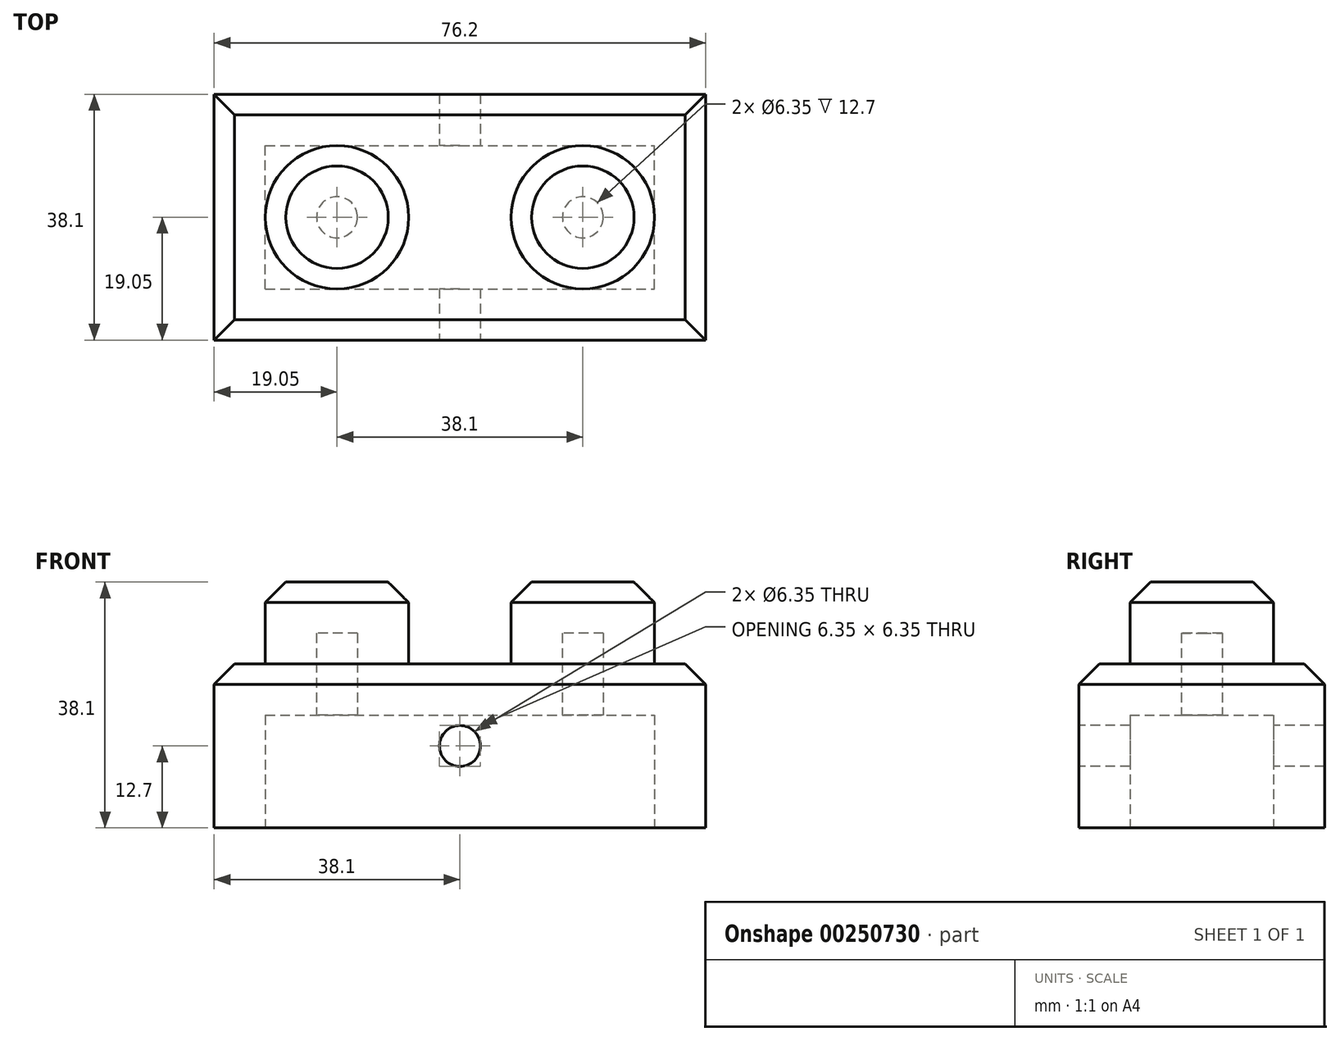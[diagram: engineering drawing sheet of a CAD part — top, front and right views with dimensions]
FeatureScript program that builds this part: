
annotation { "Feature Type Name" : "Feature", "Feature Type Description" : "" }
export const myFeature = defineFeature(function(context is Context, id is Id, definition is map)
    precondition{}
    {
        {
            var Q0;
            Q0=qCreatedBy(makeId("Top.planeOp"),FACE);
            var sketch = newSketch(context, id + "F0", { "sketchPlane" : qUnion([Q0])});
            skLineSegment(sketch, "E0.bottom", {"start": v(0, 0) * mm, "end": v(76.2, 0) * mm});
            skLineSegment(sketch, "E0.top", {"start": v(0, 38.1) * mm, "end": v(76.2, 38.1) * mm});
            skLineSegment(sketch, "E0.left", {"start": v(0, 0) * mm, "end": v(0, 38.1) * mm});
            skLineSegment(sketch, "E0.right", {"start": v(76.2, 0) * mm, "end": v(76.2, 38.1) * mm});
            skSolve(sketch);
        }
        {
            var Q0;
            Q0=makeQuery(id+"F0.imprint","IMPRINT",FACE,{"disambiguationData":[TD([[makeQuery(id+"F0.imprint","IMPRINT",EDGE,{"derivedFrom":sQuery(id+"F0.wireOp",EDGE,"E0.bottom")}),1.0]])]});
            extrude(context, id + "F1", {"entities" : qUnion([Q0]), "depth" : 25.4 * mm});
        }
        {
            var Q0;
            Q0=makeQuery(id+"F1.opExtrude","CAP_FACE",FACE,{"disambiguationData":[OSD([sQuery(id+"F0.wireOp",EDGE,"E0.bottom"),sQuery(id+"F0.wireOp",EDGE,"E0.top"),sQuery(id+"F0.wireOp",EDGE,"E0.left"),sQuery(id+"F0.wireOp",EDGE,"E0.right")])],"isStart":false});
            var sketch = newSketch(context, id + "F2", { "sketchPlane" : qUnion([Q0])});
            skCircle(sketch, "E1", {"center": v(19.05, 19.05) * mm, "radius": 11.11 * mm});
            skCircle(sketch, "E2", {"center": v(57.15, 19.05) * mm, "radius": 11.11 * mm});
            skSolve(sketch);
        }
        {
            var Q0;
            Q0 = qSketchRegion(id + "F2", true);
            extrude(context, id + "F3", {"entities" : qUnion([Q0]), "operationType" : NewBodyOperationType.ADD, "depth" : 12.7 * mm});
        }
        {
            var Q0;
            Q0=makeQuery(id+"F1.opExtrude","CAP_FACE",FACE,{"disambiguationData":[OSD([sQuery(id+"F0.wireOp",EDGE,"E0.bottom"),sQuery(id+"F0.wireOp",EDGE,"E0.top"),sQuery(id+"F0.wireOp",EDGE,"E0.left"),sQuery(id+"F0.wireOp",EDGE,"E0.right")])],"isStart":true});
            shell(context, id + "F4", {"entities" : qUnion([Q0]), "thickness" : 7.94 * mm});
        }
        {
            var Q0;
            Q0=makeQuery(id+"F1.opExtrude","SWEPT_FACE",FACE,{"disambiguationData":[OSD([sQuery(id+"F0.wireOp",EDGE,"E0.bottom")])]});
            var sketch = newSketch(context, id + "F5", { "sketchPlane" : qUnion([Q0])});
            skCircle(sketch, "E3", {"center": v(38.1, 12.7) * mm, "radius": 3.18 * mm});
            skSolve(sketch);
        }
        {
            var Q0;
            Q0=makeQuery(id+"F5.imprint","IMPRINT",FACE,{"disambiguationData":[TD([[makeQuery(id+"F5.imprint","IMPRINT",EDGE,{"derivedFrom":sQuery(id+"F5.wireOp",EDGE,"E3")}),1.0]])]});
            extrude(context, id + "F6", {"entities" : qUnion([Q0]), "operationType" : NewBodyOperationType.REMOVE, "oppositeDirection" : true, "depth" : 38.1 * mm});
        }
        {
            var Q0;
            Q0=makeQuery(id+"F3.opExtrude","CAP_FACE",FACE,{"disambiguationData":[OSD([sQuery(id+"F2.wireOp",EDGE,"E1")])],"isStart":false});
            var Q1;
            Q1=makeQuery(id+"F3.opExtrude","CAP_EDGE",EDGE,{"disambiguationData":[OSD([sQuery(id+"F2.wireOp",EDGE,"E2")])],"isStart":false});
            var Q2;
            Q2=makeQuery(id+"F1.opExtrude","CAP_EDGE",EDGE,{"disambiguationData":[OSD([sQuery(id+"F0.wireOp",EDGE,"E0.bottom")])],"isStart":false});
            var Q3;
            Q3=makeQuery(id+"F1.opExtrude","CAP_EDGE",EDGE,{"disambiguationData":[OSD([sQuery(id+"F0.wireOp",EDGE,"E0.left")])],"isStart":false});
            var Q4;
            Q4=makeQuery(id+"F1.opExtrude","CAP_EDGE",EDGE,{"disambiguationData":[OSD([sQuery(id+"F0.wireOp",EDGE,"E0.top")])],"isStart":false});
            var Q5;
            Q5=makeQuery(id+"F1.opExtrude","CAP_EDGE",EDGE,{"disambiguationData":[OSD([sQuery(id+"F0.wireOp",EDGE,"E0.right")])],"isStart":false});
            chamfer(context, id + "F7", {"entities" : qUnion([Q0, Q1, Q2, Q3, Q4, Q5]), "chamferType" : ChamferType.OFFSET_ANGLE, "width" : 3.17 * mm, "oppositeDirection" : false, "angle" : 45 * degree, "tangentPropagation" : true});
        }
    });
